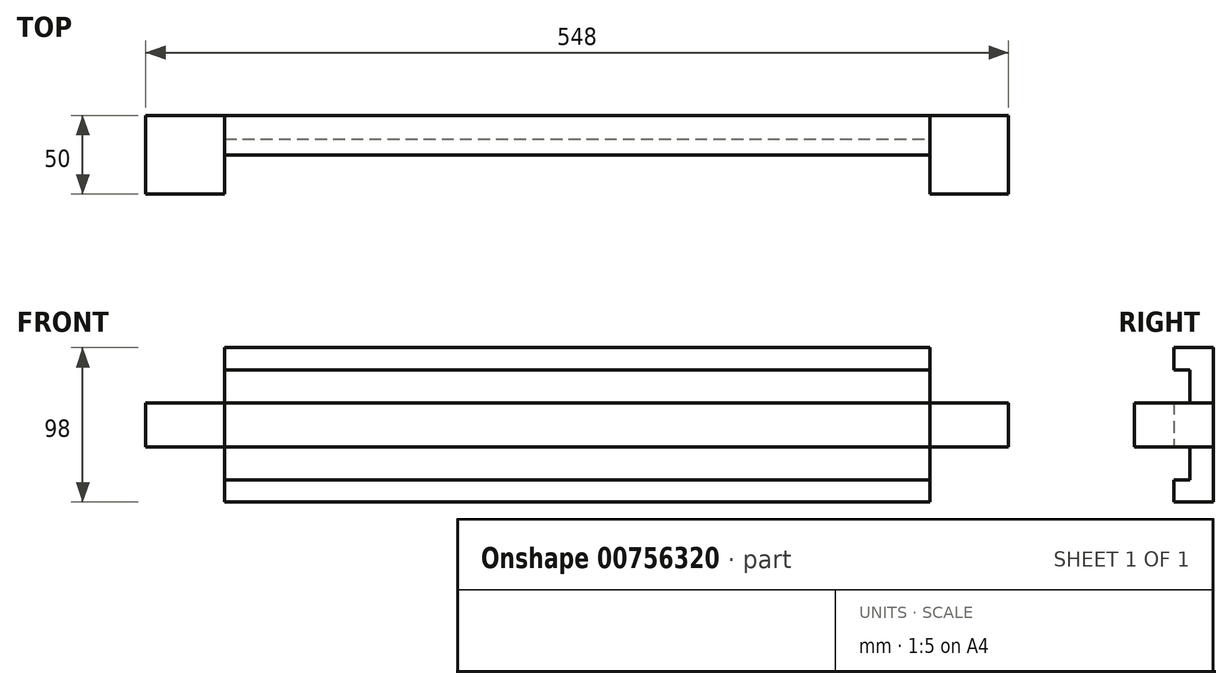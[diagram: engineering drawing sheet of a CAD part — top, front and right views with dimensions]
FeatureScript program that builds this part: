
annotation { "Feature Type Name" : "Feature", "Feature Type Description" : "" }
export const myFeature = defineFeature(function(context is Context, id is Id, definition is map)
    precondition{}
    {
        {
            var Q0;
            Q0=qCreatedBy(makeId("Front.planeOp"),FACE);
            var sketch = newSketch(context, id + "F0", { "sketchPlane" : qUnion([Q0])});
            skLineSegment(sketch, "E0.bottom", {"start": v(224, 49) * mm, "end": v(-224, 49) * mm});
            skLineSegment(sketch, "E0.left", {"start": v(274, 14) * mm, "end": v(274, 0) * mm});
            skLineSegment(sketch, "E0.right", {"start": v(-274, 14) * mm, "end": v(-274, 0) * mm});
            skPoint(sketch, "E0.middle", {"position": v(0, 0) * mm});
            skLineSegment(sketch, "E1.left", {"start": v(224, 49) * mm, "end": v(224, 0) * mm});
            skLineSegment(sketch, "E1.right", {"start": v(-224, 49) * mm, "end": v(-224, 0) * mm});
            skPoint(sketch, "E2", {"position": v(-224, 14) * mm});
            skPoint(sketch, "E3.orphan", {"position": v(-274, -49) * mm});
            skPoint(sketch, "E4.orphan", {"position": v(-224, -49) * mm});
            skPoint(sketch, "E0.top.end.orphan", {"position": v(224, -49) * mm});
            skPoint(sketch, "E5.orphan", {"position": v(274, -49) * mm});
            skLineSegment(sketch, "E6", {"start": v(-224, 14) * mm, "end": v(-274, 14) * mm});
            skLineSegment(sketch, "E7", {"start": v(224, 14) * mm, "end": v(274, 14) * mm});
            skPoint(sketch, "E8", {"position": v(-224, 35) * mm});
            skLineSegment(sketch, "E9", {"start": v(-224, 35) * mm, "end": v(224, 35) * mm});
            skLineSegment(sketch, "E10", {"start": v(-224, 14) * mm, "end": v(224, 14) * mm});
            skPoint(sketch, "E11.orphan", {"position": v(-274, 49) * mm});
            skPoint(sketch, "E12.orphan", {"position": v(274, 49) * mm});
            skLineSegment(sketch, "E13.MirrorCS", {"start": v(-224, -14) * mm, "end": v(-274, -14) * mm});
            skLineSegment(sketch, "E14.MirrorCS", {"start": v(-274, -14) * mm, "end": v(-274, 0) * mm});
            skLineSegment(sketch, "E15.MirrorCS", {"start": v(-224, -49) * mm, "end": v(-224, 0) * mm});
            skLineSegment(sketch, "E16.MirrorCS", {"start": v(224, -49) * mm, "end": v(-224, -49) * mm});
            skLineSegment(sketch, "E17.MirrorCS", {"start": v(224, -49) * mm, "end": v(224, 0) * mm});
            skLineSegment(sketch, "E18.MirrorCS", {"start": v(274, -14) * mm, "end": v(274, 0) * mm});
            skLineSegment(sketch, "E19.MirrorCS", {"start": v(224, -14) * mm, "end": v(274, -14) * mm});
            skLineSegment(sketch, "E20.MirrorCS", {"start": v(-224, -35) * mm, "end": v(224, -35) * mm});
            skLineSegment(sketch, "E21.MirrorCS", {"start": v(-224, -14) * mm, "end": v(224, -14) * mm});
            skSolve(sketch);
        }
        {
            var Q0;
            {var subQ0=sQuery(id+"F0.wireOp",EDGE,"E0.bottom");Q0=makeQuery(id+"F0.imprint","IMPRINT",FACE,{"disambiguationData":[TD([[makeQuery(id+"F0.imprint","IMPRINT",EDGE,{"derivedFrom":subQ0}),1.0]])]});}
            var Q1;
            {var subQ0=sQuery(id+"F0.wireOp",EDGE,"E16.MirrorCS");Q1=makeQuery(id+"F0.imprint","IMPRINT",FACE,{"disambiguationData":[TD([[makeQuery(id+"F0.imprint","IMPRINT",EDGE,{"derivedFrom":subQ0}),-1.0]])]});}
            var Q2;
            Q2=makeQuery(id+"F0.imprint","IMPRINT",FACE,{"disambiguationData":[TD([[makeQuery(id+"F0.imprint","IMPRINT",EDGE,{"derivedFrom":sQuery(id+"F0.wireOp",EDGE,"E0.right")}),1.0]])]});
            var Q3;
            Q3=makeQuery(id+"F0.imprint","IMPRINT",FACE,{"disambiguationData":[TD([[makeQuery(id+"F0.imprint","IMPRINT",EDGE,{"derivedFrom":sQuery(id+"F0.wireOp",EDGE,"E0.left")}),-1.0]])]});
            var Q4;
            {var subQ2=sQuery(id+"F0.wireOp",EDGE,"E9");Q4=makeQuery(id+"F0.imprint","IMPRINT",FACE,{"disambiguationData":[TD([[makeQuery(id+"F0.imprint","IMPRINT",EDGE,{"derivedFrom":subQ2}),-1.0]])]});}
            var Q5;
            {var subQ4=sQuery(id+"F0.wireOp",EDGE,"E10");Q5=makeQuery(id+"F0.imprint","IMPRINT",FACE,{"disambiguationData":[TD([[makeQuery(id+"F0.imprint","IMPRINT",EDGE,{"derivedFrom":subQ4}),-1.0]])]});}
            var Q6;
            {var subQ2=sQuery(id+"F0.wireOp",EDGE,"E20.MirrorCS");Q6=makeQuery(id+"F0.imprint","IMPRINT",FACE,{"disambiguationData":[TD([[makeQuery(id+"F0.imprint","IMPRINT",EDGE,{"derivedFrom":subQ2}),1.0]])]});}
            extrude(context, id + "F1", {"entities" : qUnion([Q0, Q1, Q2, Q3, Q4, Q5, Q6]), "depth" : 25 * mm, "offsetDistance" : 25 * mm});
        }
        {
            var Q0;
            Q0=makeQuery(id+"F1.opExtrude","CAP_FACE",FACE,{"disambiguationData":[OSD([sQuery(id+"F0.wireOp",EDGE,"E0.left"),sQuery(id+"F0.wireOp",EDGE,"E0.right"),sQuery(id+"F0.wireOp",EDGE,"E0.bottom"),sQuery(id+"F0.wireOp",EDGE,"E1.left"),sQuery(id+"F0.wireOp",EDGE,"E1.right"),sQuery(id+"F0.wireOp",EDGE,"E6"),sQuery(id+"F0.wireOp",EDGE,"E7"),sQuery(id+"F0.wireOp",EDGE,"E13.MirrorCS"),sQuery(id+"F0.wireOp",EDGE,"E14.MirrorCS"),sQuery(id+"F0.wireOp",EDGE,"E15.MirrorCS"),sQuery(id+"F0.wireOp",EDGE,"E16.MirrorCS"),sQuery(id+"F0.wireOp",EDGE,"E17.MirrorCS"),sQuery(id+"F0.wireOp",EDGE,"E18.MirrorCS"),sQuery(id+"F0.wireOp",EDGE,"E19.MirrorCS")])],"isStart":false});
            var sketch = newSketch(context, id + "F2", { "sketchPlane" : qUnion([Q0])});
            skLineSegment(sketch, "E22", {"start": v(-224, 14) * mm, "end": v(-224, 31.5) * mm});
            skLineSegment(sketch, "E23", {"start": v(-224, 31.5) * mm, "end": v(-224, 35) * mm});
            skLineSegment(sketch, "E24", {"start": v(-224, 35) * mm, "end": v(224, 35) * mm});
            skLineSegment(sketch, "E25", {"start": v(-224, 14) * mm, "end": v(224, 14) * mm});
            skLineSegment(sketch, "E26", {"start": v(-224, -14) * mm, "end": v(224, -14) * mm});
            skLineSegment(sketch, "E27", {"start": v(-224, -14) * mm, "end": v(-224, -35) * mm});
            skLineSegment(sketch, "E28", {"start": v(-224, -35) * mm, "end": v(224, -35) * mm});
            skSolve(sketch);
        }
        {
            var Q0;
            Q0 = qSketchRegion(id + "F2", true);
            var Q1;
            Q1=makeQuery(id+"F2.imprint","IMPRINT",FACE,{"disambiguationData":[TD([[makeQuery(id+"F2.imprint","IMPRINT",EDGE,{"derivedFrom":sQuery(id+"F2.wireOp",EDGE,"E22")}),1.0]])]});
            var Q2;
            {var subQ0=sQuery(id+"F2.wireOp",EDGE,"E26");Q2=makeQuery(id+"F2.imprint","IMPRINT",FACE,{"disambiguationData":[TD([[makeQuery(id+"F2.imprint","IMPRINT",EDGE,{"derivedFrom":subQ0}),-1.0]])]});}
            extrude(context, id + "F3", {"entities" : qUnion([Q0, Q1, Q2]), "operationType" : NewBodyOperationType.REMOVE, "oppositeDirection" : true, "depth" : 10 * mm, "offsetDistance" : 25 * mm});
        }
        {
            var Q0;
            {var subQ0=sQuery(id+"F0.wireOp",EDGE,"E7");var subQ1=sQuery(id+"F0.wireOp",EDGE,"E14.MirrorCS");var subQ2=sQuery(id+"F0.wireOp",EDGE,"E0.right");var subQ3=sQuery(id+"F0.wireOp",EDGE,"E6");var subQ4=sQuery(id+"F0.wireOp",EDGE,"E18.MirrorCS");var subQ5=sQuery(id+"F0.wireOp",EDGE,"E0.left");var subQ6=sQuery(id+"F0.wireOp",EDGE,"E19.MirrorCS");var subQ7=sQuery(id+"F0.wireOp",EDGE,"E13.MirrorCS");Q0=makeQuery(id+"F3.boolean.opBoolean","SPLIT",FACE,{"disambiguationData":[TD([makeQuery(id+"F1.opExtrude","SWEPT_FACE",FACE,{"disambiguationData":[OSD([subQ3])]})])],"derivedFrom":makeQuery(id+"F1.opExtrude","CAP_FACE",FACE,{"disambiguationData":[OSD([subQ5,subQ2,sQuery(id+"F0.wireOp",EDGE,"E0.bottom"),sQuery(id+"F0.wireOp",EDGE,"E1.left"),sQuery(id+"F0.wireOp",EDGE,"E1.right"),subQ3,subQ0,subQ7,subQ1,sQuery(id+"F0.wireOp",EDGE,"E15.MirrorCS"),sQuery(id+"F0.wireOp",EDGE,"E16.MirrorCS"),sQuery(id+"F0.wireOp",EDGE,"E17.MirrorCS"),subQ4,subQ6])],"isStart":false})});}
            var sketch = newSketch(context, id + "F4", { "sketchPlane" : qUnion([Q0])});
            skLineSegment(sketch, "E29", {"start": v(-274, 14) * mm, "end": v(-224, 14) * mm});
            skLineSegment(sketch, "E30", {"start": v(-224, 14) * mm, "end": v(-224, -14) * mm});
            skLineSegment(sketch, "E31", {"start": v(-224, -14) * mm, "end": v(-274, -14) * mm});
            skLineSegment(sketch, "E32", {"start": v(-274, -14) * mm, "end": v(-274, 14) * mm});
            skLineSegment(sketch, "E33", {"start": v(274, 14) * mm, "end": v(224, 14) * mm});
            skLineSegment(sketch, "E34", {"start": v(224, 14) * mm, "end": v(224, -14) * mm});
            skLineSegment(sketch, "E35", {"start": v(224, -14) * mm, "end": v(274, -14) * mm});
            skLineSegment(sketch, "E36", {"start": v(274, -14) * mm, "end": v(274, 14) * mm});
            skSolve(sketch);
        }
        {
            var Q0;
            Q0=makeQuery(id+"F4.imprint","IMPRINT",FACE,{"disambiguationData":[TD([[makeQuery(id+"F4.imprint","IMPRINT",EDGE,{"derivedFrom":sQuery(id+"F4.wireOp",EDGE,"E33")}),1.0]])]});
            var Q1;
            Q1=makeQuery(id+"F4.imprint","IMPRINT",FACE,{"disambiguationData":[TD([[makeQuery(id+"F4.imprint","IMPRINT",EDGE,{"derivedFrom":sQuery(id+"F4.wireOp",EDGE,"E29")}),1.0]])]});
            extrude(context, id + "F5", {"entities" : qUnion([Q0, Q1]), "operationType" : NewBodyOperationType.ADD, "depth" : 25 * mm, "offsetDistance" : 25 * mm});
        }
    });
